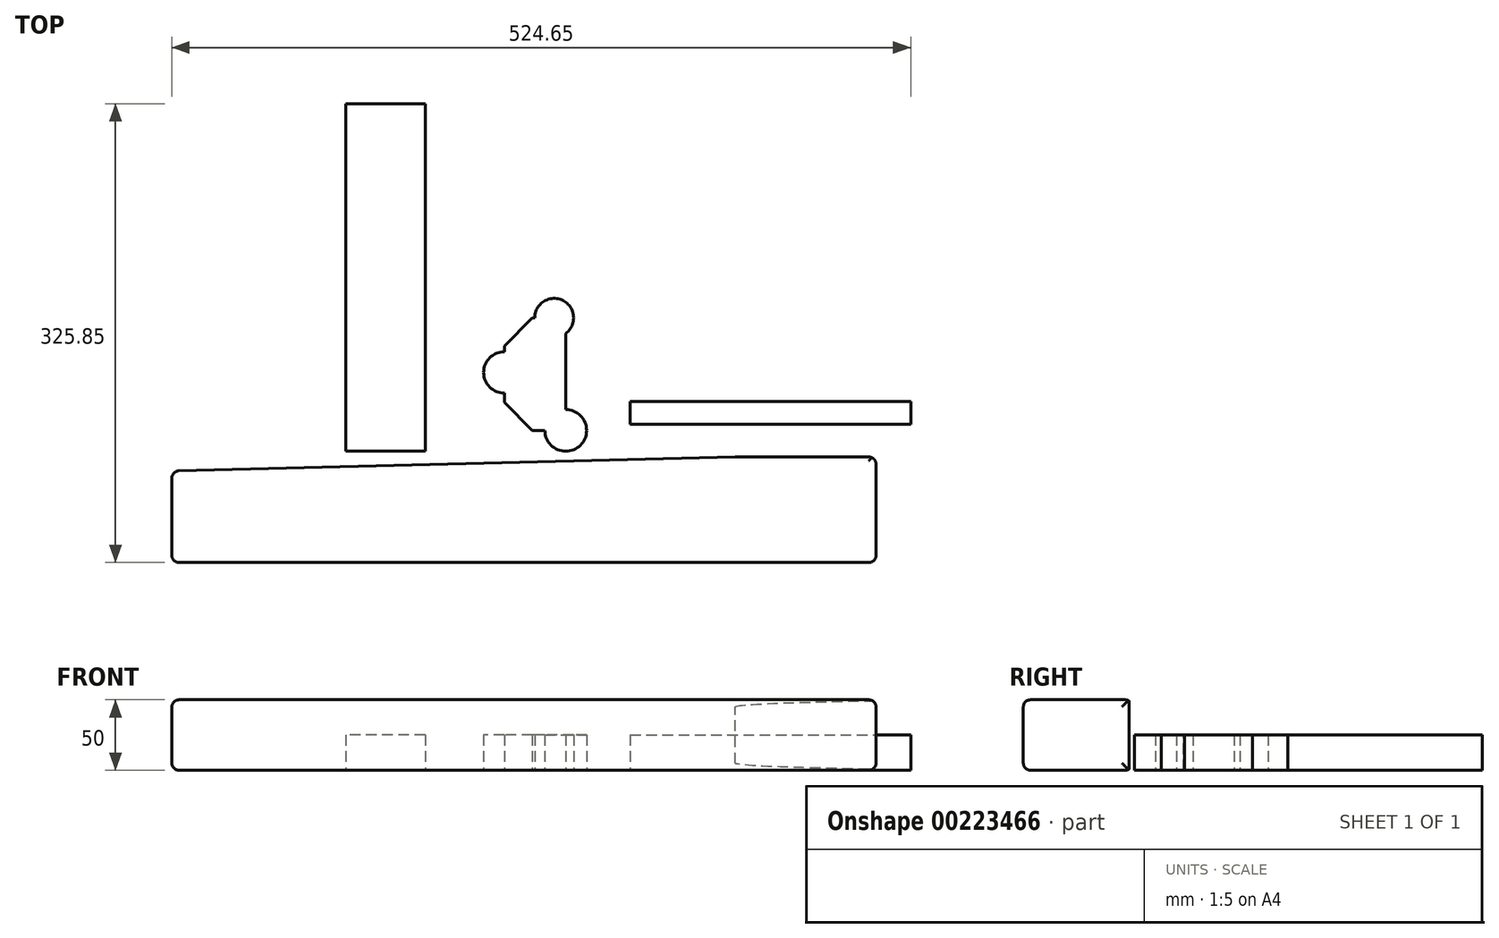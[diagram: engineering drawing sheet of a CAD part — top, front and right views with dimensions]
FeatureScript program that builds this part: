
annotation { "Feature Type Name" : "Feature", "Feature Type Description" : "" }
export const myFeature = defineFeature(function(context is Context, id is Id, definition is map)
    precondition{}
    {
        {
            var Q0;
            Q0=qCreatedBy(makeId("Top.planeOp"),FACE);
            var sketch = newSketch(context, id + "F0", { "sketchPlane" : qUnion([Q0])});
            skLineSegment(sketch, "E0.bottom", {"start": v(-231.19, -34.8) * mm, "end": v(268.81, -34.8) * mm});
            skLineSegment(sketch, "E0.top", {"start": v(-231.19, 40.2) * mm, "end": v(268.81, 40.2) * mm});
            skLineSegment(sketch, "E0.left", {"start": v(-231.19, -34.8) * mm, "end": v(-231.19, 40.2) * mm});
            skLineSegment(sketch, "E0.right", {"start": v(268.81, -34.8) * mm, "end": v(268.81, 40.2) * mm});
            skSolve(sketch);
        }
        {
            var Q0;
            Q0 = qSketchRegion(id + "F0", true);
            extrude(context, id + "F1", {"entities" : qUnion([Q0]), "depth" : 50 * mm});
        }
        {
            var Q0;
            Q0=makeQuery(id+"F1.opExtrude","SWEPT_EDGE",EDGE,{"disambiguationData":[OSD([sQuery(id+"F0.wireOp",EDGE,"E0.top"),sQuery(id+"F0.wireOp",EDGE,"E0.left")])]});
            chamfer(context, id + "F2", {"entities" : qUnion([Q0]), "chamferType" : ChamferType.TWO_OFFSETS, "width1" : 10 * mm, "oppositeDirection" : false, "width2" : 400 * mm, "tangentPropagation" : true});
        }
        {
            var Q0;
            {var subQ0=sQuery(id+"F0.wireOp",EDGE,"E0.left");Q0=makeQuery(id+"F2.opChamfer","BLEND_EDGE",EDGE,{"blendedFrom":[makeQuery(id+"F1.opExtrude","SWEPT_EDGE",EDGE,{"disambiguationData":[OSD([sQuery(id+"F0.wireOp",EDGE,"E0.top"),subQ0])]}),makeQuery(id+"F1.opExtrude","SWEPT_FACE",FACE,{"disambiguationData":[OSD([subQ0])]})],"blendedInto":[makeQuery(id+"F1.opExtrude","SWEPT_FACE",FACE,{"disambiguationData":[OSD([subQ0])]})]});}
            var Q1;
            {var subQ0=sQuery(id+"F0.wireOp",EDGE,"E0.left");var subQ1=sQuery(id+"F0.wireOp",EDGE,"E0.top");Q1=makeQuery(id+"F2.opChamfer","BLEND_EDGE",EDGE,{"blendedFrom":[makeQuery(id+"F1.opExtrude","SWEPT_EDGE",EDGE,{"disambiguationData":[OSD([subQ1,subQ0])]}),makeQuery(id+"F1.opExtrude","CAP_FACE",FACE,{"disambiguationData":[OSD([sQuery(id+"F0.wireOp",EDGE,"E0.bottom"),subQ1,subQ0,sQuery(id+"F0.wireOp",EDGE,"E0.right")])],"isStart":false})],"blendedInto":[makeQuery(id+"F1.opExtrude","CAP_FACE",FACE,{"disambiguationData":[OSD([sQuery(id+"F0.wireOp",EDGE,"E0.bottom"),subQ1,subQ0,sQuery(id+"F0.wireOp",EDGE,"E0.right")])],"isStart":false})]});}
            var Q2;
            Q2=makeQuery(id+"F1.opExtrude","CAP_EDGE",EDGE,{"disambiguationData":[OSD([sQuery(id+"F0.wireOp",EDGE,"E0.left")])],"isStart":false});
            var Q3;
            Q3=makeQuery(id+"F1.opExtrude","CAP_EDGE",EDGE,{"disambiguationData":[OSD([sQuery(id+"F0.wireOp",EDGE,"E0.left")])],"isStart":true});
            var Q4;
            {var subQ0=sQuery(id+"F0.wireOp",EDGE,"E0.left");var subQ1=sQuery(id+"F0.wireOp",EDGE,"E0.top");Q4=makeQuery(id+"F2.opChamfer","BLEND_EDGE",EDGE,{"blendedFrom":[makeQuery(id+"F1.opExtrude","SWEPT_EDGE",EDGE,{"disambiguationData":[OSD([subQ1,subQ0])]}),makeQuery(id+"F1.opExtrude","CAP_FACE",FACE,{"disambiguationData":[OSD([sQuery(id+"F0.wireOp",EDGE,"E0.bottom"),subQ1,subQ0,sQuery(id+"F0.wireOp",EDGE,"E0.right")])],"isStart":true})],"blendedInto":[makeQuery(id+"F1.opExtrude","CAP_FACE",FACE,{"disambiguationData":[OSD([sQuery(id+"F0.wireOp",EDGE,"E0.bottom"),subQ1,subQ0,sQuery(id+"F0.wireOp",EDGE,"E0.right")])],"isStart":true})]});}
            var Q5;
            Q5=makeQuery(id+"F1.opExtrude","CAP_EDGE",EDGE,{"disambiguationData":[OSD([sQuery(id+"F0.wireOp",EDGE,"E0.bottom")])],"isStart":false});
            var Q6;
            Q6=makeQuery(id+"F1.opExtrude","SWEPT_EDGE",EDGE,{"disambiguationData":[OSD([sQuery(id+"F0.wireOp",EDGE,"E0.bottom"),sQuery(id+"F0.wireOp",EDGE,"E0.left")])]});
            var Q7;
            Q7=makeQuery(id+"F1.opExtrude","CAP_EDGE",EDGE,{"disambiguationData":[OSD([sQuery(id+"F0.wireOp",EDGE,"E0.right")])],"isStart":false});
            var Q8;
            Q8=makeQuery(id+"F1.opExtrude","SWEPT_EDGE",EDGE,{"disambiguationData":[OSD([sQuery(id+"F0.wireOp",EDGE,"E0.top"),sQuery(id+"F0.wireOp",EDGE,"E0.right")])]});
            var Q9;
            Q9=makeQuery(id+"F1.opExtrude","SWEPT_EDGE",EDGE,{"disambiguationData":[OSD([sQuery(id+"F0.wireOp",EDGE,"E0.bottom"),sQuery(id+"F0.wireOp",EDGE,"E0.right")])]});
            var Q10;
            Q10=makeQuery(id+"F1.opExtrude","CAP_EDGE",EDGE,{"disambiguationData":[OSD([sQuery(id+"F0.wireOp",EDGE,"E0.right")])],"isStart":true});
            var Q11;
            Q11=makeQuery(id+"F1.opExtrude","CAP_EDGE",EDGE,{"disambiguationData":[OSD([sQuery(id+"F0.wireOp",EDGE,"E0.bottom")])],"isStart":true});
            fillet(context, id + "F3", {"entities" : qUnion([Q0, Q1, Q2, Q3, Q4, Q5, Q6, Q7, Q8, Q9, Q10, Q11]), "radius" : 5 * mm, "tangentPropagation" : true, "allowEdgeOverflow" : false});
        }
        {
            var Q0;
            Q0=qCreatedBy(makeId("Top.planeOp"),FACE);
            var sketch = newSketch(context, id + "F4", { "sketchPlane" : qUnion([Q0])});
            skCircle(sketch, "E1", {"center": v(48.5, 59.06) * mm, "radius": 14.83 * mm});
            skCircle(sketch, "E2", {"center": v(4.85, 100.27) * mm, "radius": 14.68 * mm});
            skCircle(sketch, "E3", {"center": v(40.26, 139.03) * mm, "radius": 13.82 * mm});
            skLineSegment(sketch, "E4.bottom", {"start": v(48.5, 59.06) * mm, "end": v(4.85, 59.06) * mm});
            skLineSegment(sketch, "E4.top", {"start": v(48.5, 100.27) * mm, "end": v(4.85, 100.27) * mm});
            skLineSegment(sketch, "E4.left", {"start": v(48.5, 59.06) * mm, "end": v(48.5, 100.27) * mm});
            skLineSegment(sketch, "E4.right", {"start": v(4.85, 59.06) * mm, "end": v(4.85, 100.27) * mm});
            skLineSegment(sketch, "E5.bottom", {"start": v(40.26, 139.03) * mm, "end": v(4.85, 139.03) * mm});
            skLineSegment(sketch, "E5.top", {"start": v(40.26, 100.27) * mm, "end": v(4.85, 100.27) * mm});
            skLineSegment(sketch, "E5.left", {"start": v(40.26, 139.03) * mm, "end": v(40.26, 100.27) * mm});
            skLineSegment(sketch, "E5.right", {"start": v(4.85, 139.03) * mm, "end": v(4.85, 100.27) * mm});
            skLineSegment(sketch, "E6.bottom", {"start": v(48.5, 59.06) * mm, "end": v(40.26, 59.06) * mm});
            skLineSegment(sketch, "E6.top", {"start": v(48.5, 139.03) * mm, "end": v(40.26, 139.03) * mm});
            skLineSegment(sketch, "E6.left", {"start": v(48.5, 59.06) * mm, "end": v(48.5, 139.03) * mm});
            skLineSegment(sketch, "E6.right", {"start": v(40.26, 59.06) * mm, "end": v(40.26, 139.03) * mm});
            skSolve(sketch);
        }
        {
            var Q0;
            Q0 = qSketchRegion(id + "F4", true);
            extrude(context, id + "F5", {"entities" : qUnion([Q0]), "depth" : 25 * mm});
        }
        {
            var Q0;
            Q0=makeQuery(id+"F5.opExtrude","SWEPT_EDGE",EDGE,{"disambiguationData":[OSD([sQuery(id+"F4.wireOp",EDGE,"E4.bottom"),sQuery(id+"F4.wireOp",EDGE,"E4.right")])]});
            var Q1;
            Q1=makeQuery(id+"F5.opExtrude","SWEPT_EDGE",EDGE,{"disambiguationData":[OSD([sQuery(id+"F4.wireOp",EDGE,"E5.bottom"),sQuery(id+"F4.wireOp",EDGE,"E5.right")])]});
            chamfer(context, id + "F6", {"entities" : qUnion([Q0, Q1]), "width" : 20 * mm, "tangentPropagation" : true});
        }
        {
            var Q0;
            Q0=qCreatedBy(makeId("Top.planeOp"),FACE);
            var sketch = newSketch(context, id + "F7", { "sketchPlane" : qUnion([Q0])});
            skLineSegment(sketch, "E7.bottom", {"start": v(-51.36, 44.27) * mm, "end": v(-107.8, 44.27) * mm});
            skLineSegment(sketch, "E7.top", {"start": v(-51.36, 291.05) * mm, "end": v(-107.8, 291.05) * mm});
            skLineSegment(sketch, "E7.left", {"start": v(-51.36, 44.27) * mm, "end": v(-51.36, 291.05) * mm});
            skLineSegment(sketch, "E7.right", {"start": v(-107.8, 44.27) * mm, "end": v(-107.8, 291.05) * mm});
            skSolve(sketch);
        }
        {
            var Q0;
            Q0 = qSketchRegion(id + "F7", true);
            extrude(context, id + "F8", {"entities" : qUnion([Q0]), "depth" : 25 * mm});
        }
        {
            var Q0;
            Q0=qCreatedBy(makeId("Top.planeOp"),FACE);
            var sketch = newSketch(context, id + "F9", { "sketchPlane" : qUnion([Q0])});
            skLineSegment(sketch, "E8.bottom", {"start": v(94.21, 63.28) * mm, "end": v(293.46, 63.28) * mm});
            skLineSegment(sketch, "E8.top", {"start": v(94.21, 79.66) * mm, "end": v(293.46, 79.66) * mm});
            skLineSegment(sketch, "E8.left", {"start": v(94.21, 63.28) * mm, "end": v(94.21, 79.66) * mm});
            skLineSegment(sketch, "E8.right", {"start": v(293.46, 63.28) * mm, "end": v(293.46, 79.66) * mm});
            skSolve(sketch);
        }
        {
            var Q0;
            Q0 = qSketchRegion(id + "F9", true);
            extrude(context, id + "F10", {"entities" : qUnion([Q0]), "depth" : 25 * mm});
        }
    });
